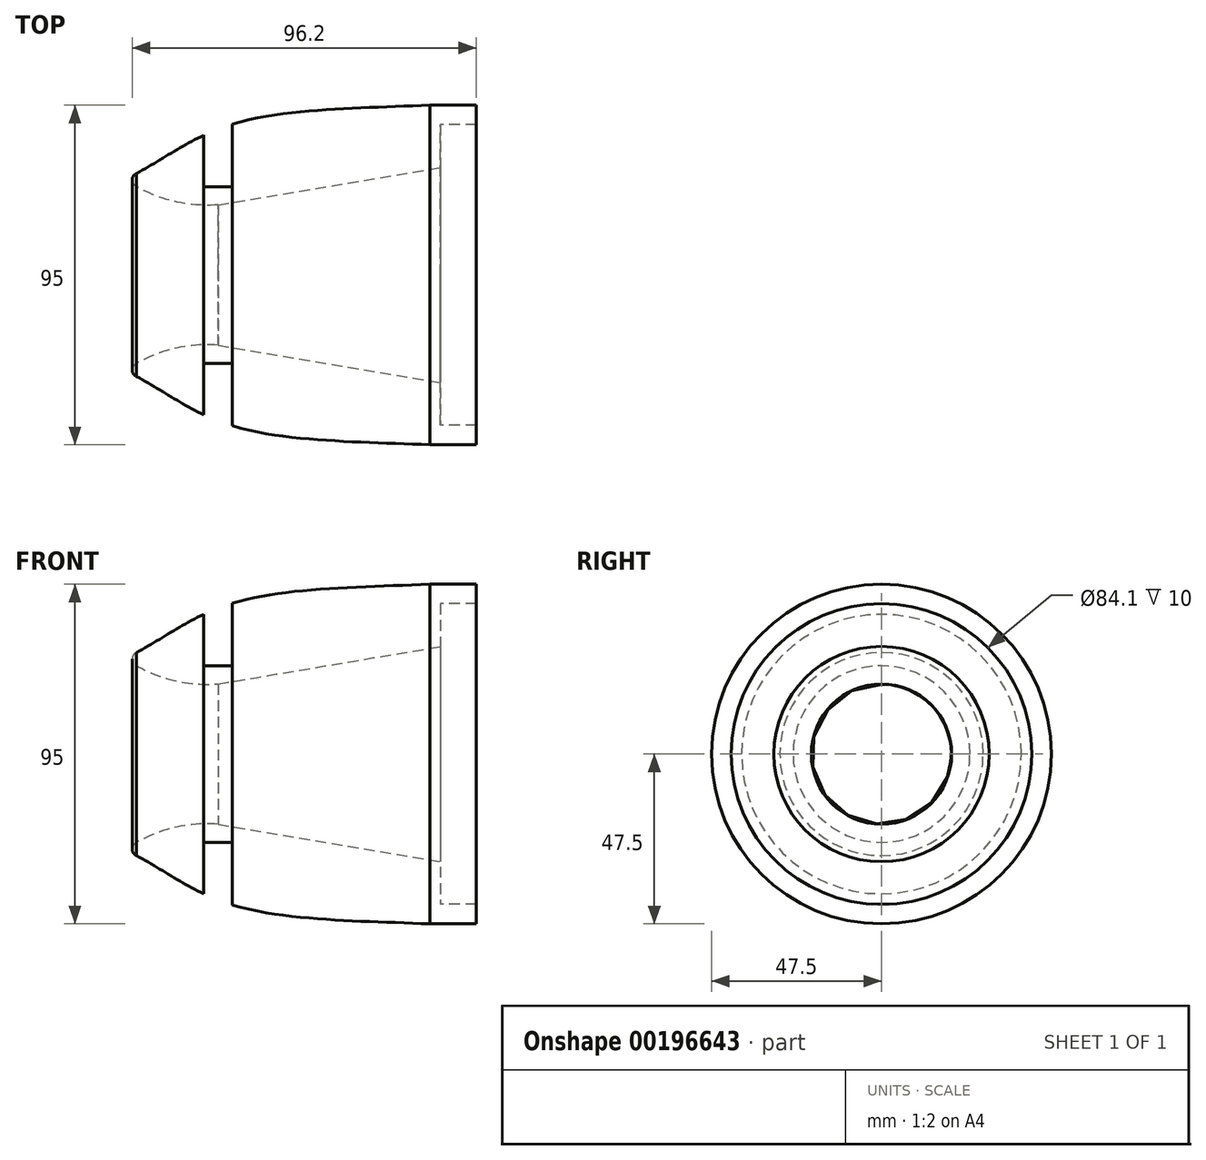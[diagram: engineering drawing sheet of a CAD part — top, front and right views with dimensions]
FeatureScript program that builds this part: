
annotation { "Feature Type Name" : "Feature", "Feature Type Description" : "" }
export const myFeature = defineFeature(function(context is Context, id is Id, definition is map)
    precondition{}
    {
        {
            var Q0;
            Q0=qCreatedBy(makeId("Front.planeOp"),FACE);
            var sketch = newSketch(context, id + "F0", { "sketchPlane" : qUnion([Q0])});
            skArc(sketch, "E0", {"start": v(4, 24.86) * mm, "mid": v(15.1, 20.5) * mm, "end": v(27, 19.61) * mm});
            skLineSegment(sketch, "E1", {"start": v(27, 19.61) * mm, "end": v(89.2, 30.1) * mm});
            skLineSegment(sketch, "E2", {"start": v(89.2, 30.1) * mm, "end": v(89.2, 42.05) * mm});
            skLineSegment(sketch, "E3", {"start": v(89.2, 42.05) * mm, "end": v(99.2, 42.05) * mm});
            skLineSegment(sketch, "E4", {"start": v(99.2, 42.05) * mm, "end": v(99.2, 47.5) * mm});
            skLineSegment(sketch, "E5", {"start": v(99.2, 47.5) * mm, "end": v(86.2, 47.5) * mm});
            skLineSegment(sketch, "E6", {"start": v(86.2, 47.5) * mm, "end": v(86.2, -152.5) * mm, "construction": true});
            skLineSegment(sketch, "E7", {"start": v(0, 0) * mm, "end": v(78.27, 0) * mm, "construction": true});
            skLineSegment(sketch, "E8", {"start": v(78.27, 0) * mm, "end": v(78.27, -5.25) * mm, "construction": true});
            skPoint(sketch, "E9.visualSharp", {"position": v(1.2, 26.63) * mm});
            skArc(sketch, "E9.filletArc", {"start": v(4.18, 28.41) * mm, "mid": v(3, 26.7) * mm, "end": v(4, 24.86) * mm});
            skLineSegment(sketch, "E10", {"start": v(27, 19.61) * mm, "end": v(27, 38.39) * mm, "construction": true});
            skFitSpline(sketch, "E11", {"points": [v(4.18, 28.41) * mm, v(30.54, 42.05) * mm, v(86.2, 47.5) * mm], "startDerivative": vector(60.54, 31.9) * mm, "endDerivative": vector(101.5, 4.43) * mm});
            skLineSegment(sketch, "E12.bottom", {"start": v(23, 42.48) * mm, "end": v(31, 42.48) * mm});
            skLineSegment(sketch, "E12.top", {"start": v(23, 24.7) * mm, "end": v(31, 24.7) * mm});
            skLineSegment(sketch, "E12.left", {"start": v(23, 42.48) * mm, "end": v(23, 24.7) * mm});
            skLineSegment(sketch, "E12.right", {"start": v(31, 42.48) * mm, "end": v(31, 24.7) * mm});
            skPoint(sketch, "E12.middle", {"position": v(27, 33.6) * mm});
            skSolve(sketch);
        }
        {
            var Q0;
            Q0=makeQuery(id+"F0.imprint","IMPRINT",FACE,{"disambiguationData":[TD([[makeQuery(id+"F0.imprint","IMPRINT",EDGE,{"derivedFrom":sQuery(id+"F0.wireOp",EDGE,"E0")}),1.0]])]});
            var Q1;
            Q1=sQuery(id+"F0.wireOp",EDGE,"E7");
            revolve(context, id + "F1", {"entities" : qUnion([Q0]), "axis" : qUnion([Q1]), "revolveType" : RevolveType.FULL});
        }
    });
